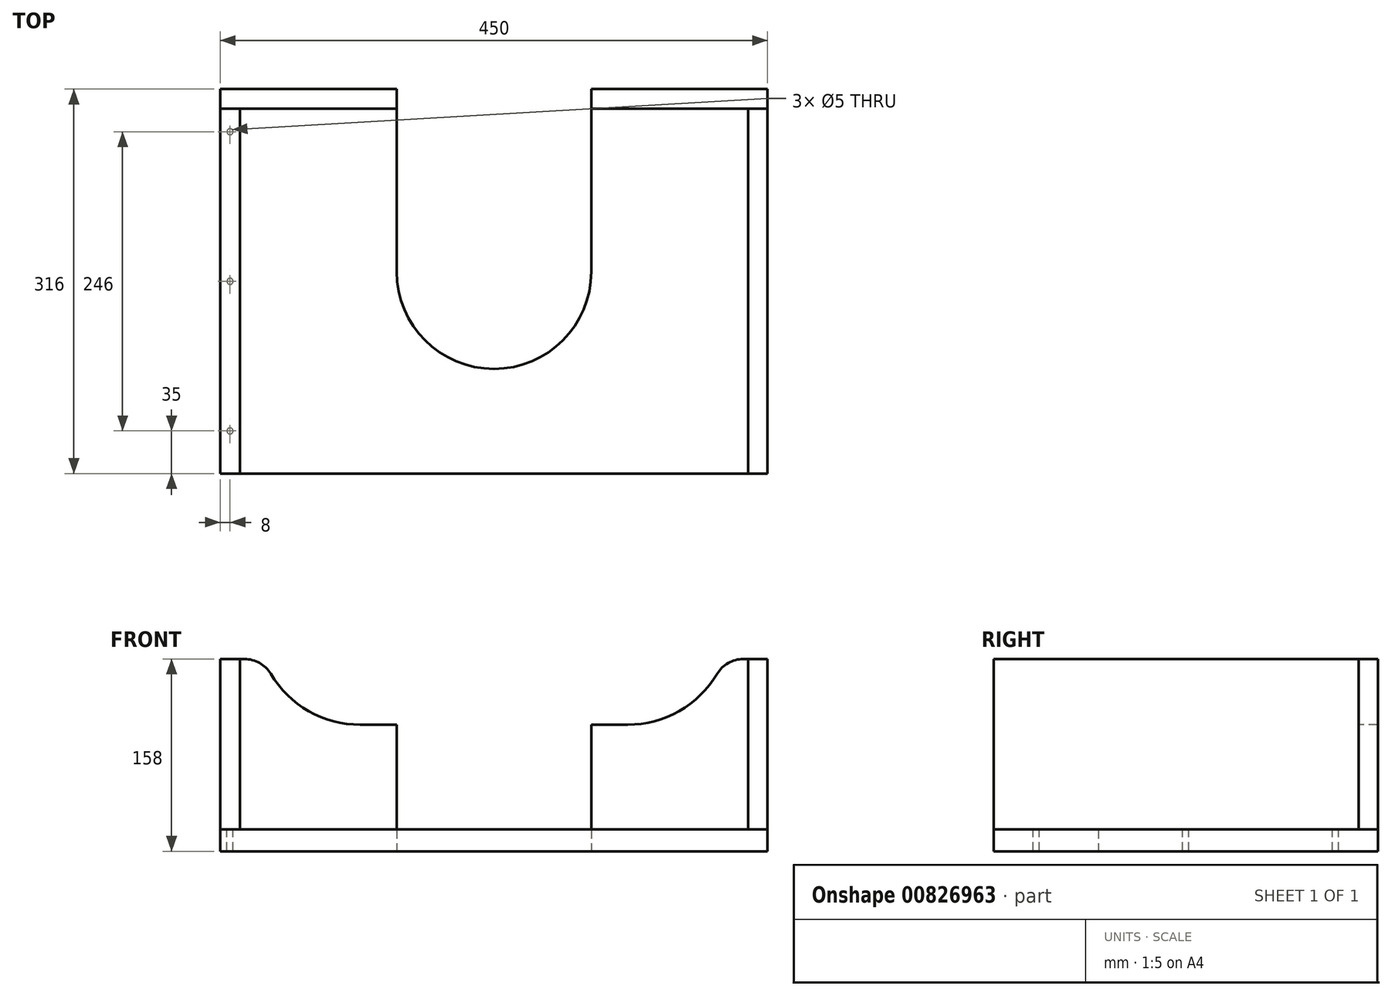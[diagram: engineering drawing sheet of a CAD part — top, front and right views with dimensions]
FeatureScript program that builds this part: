
annotation { "Feature Type Name" : "Feature", "Feature Type Description" : "" }
export const myFeature = defineFeature(function(context is Context, id is Id, definition is map)
    precondition{}
    {
        {
            var Q0;
            Q0=qCreatedBy(makeId("Front.planeOp"),FACE);
            var sketch = newSketch(context, id + "F0", { "sketchPlane" : qUnion([Q0])});
            skLineSegment(sketch, "E0.bottom", {"start": v(225, 70) * mm, "end": v(-225, 70) * mm});
            skLineSegment(sketch, "E0.top", {"start": v(225, -70) * mm, "end": v(-225, -70) * mm});
            skLineSegment(sketch, "E0.left", {"start": v(225, 70) * mm, "end": v(225, -70) * mm});
            skLineSegment(sketch, "E0.right", {"start": v(-225, 70) * mm, "end": v(-225, -70) * mm});
            skPoint(sketch, "E0.middle", {"position": v(0, 0) * mm});
            skSolve(sketch);
        }
        {
            var Q0;
            Q0=makeQuery(id+"F0.imprint","IMPRINT",FACE,{"disambiguationData":[TD([[makeQuery(id+"F0.imprint","IMPRINT",EDGE,{"derivedFrom":sQuery(id+"F0.wireOp",EDGE,"E0.bottom")}),1.0]])]});
            extrude(context, id + "F1", {"entities" : qUnion([Q0]), "depth" : 16 * mm, "offsetDistance" : 25 * mm});
        }
        {
            var Q0;
            Q0=makeQuery(id+"F1.opExtrude","CAP_FACE",FACE,{"disambiguationData":[OSD([sQuery(id+"F0.wireOp",EDGE,"E0.bottom"),sQuery(id+"F0.wireOp",EDGE,"E0.top"),sQuery(id+"F0.wireOp",EDGE,"E0.left"),sQuery(id+"F0.wireOp",EDGE,"E0.right")])],"isStart":false});
            var sketch = newSketch(context, id + "F2", { "sketchPlane" : qUnion([Q0])});
            skLineSegment(sketch, "E1", {"start": v(-225, 70) * mm, "end": v(-205, 70) * mm});
            skArc(sketch, "E2", {"start": v(-183.52, 57.79) * mm, "mid": v(-192.65, 66.73) * mm, "end": v(-205, 70) * mm});
            skArc(sketch, "E3", {"start": v(-183.52, 57.79) * mm, "mid": v(-152.28, 27.18) * mm, "end": v(-110, 16) * mm});
            skLineSegment(sketch, "E4", {"start": v(-110, 16) * mm, "end": v(0, 16) * mm});
            skLineSegment(sketch, "E5", {"start": v(0, 70) * mm, "end": v(0, -70) * mm, "construction": true});
            skLineSegment(sketch, "E6.MirrorCS", {"start": v(225, 70) * mm, "end": v(205, 70) * mm});
            skLineSegment(sketch, "E7.MirrorCS", {"start": v(110, 16) * mm, "end": v(0, 16) * mm});
            skArc(sketch, "E8.MirrorCS", {"start": v(183.52, 57.79) * mm, "mid": v(152.28, 27.18) * mm, "end": v(110, 16) * mm});
            skArc(sketch, "E9.MirrorCS", {"start": v(183.52, 57.79) * mm, "mid": v(192.65, 66.73) * mm, "end": v(205, 70) * mm});
            skSolve(sketch);
        }
        {
            var Q0;
            {var subQ0=sQuery(id+"F2.wireOp",EDGE,"E2");Q0=makeQuery(id+"F2.imprint","IMPRINT",FACE,{"disambiguationData":[TD([[makeQuery(id+"F2.imprint","IMPRINT",EDGE,{"derivedFrom":subQ0}),-1.0]])]});}
            extrude(context, id + "F3", {"entities" : qUnion([Q0]), "operationType" : NewBodyOperationType.REMOVE, "endBound" : BoundingType.THROUGH_ALL, "oppositeDirection" : true, "depth" : 25 * mm, "offsetDistance" : 25 * mm});
        }
        {
            var Q0;
            Q0=makeQuery(id+"F1.opExtrude","CAP_FACE",FACE,{"disambiguationData":[OSD([sQuery(id+"F0.wireOp",EDGE,"E0.bottom"),sQuery(id+"F0.wireOp",EDGE,"E0.top"),sQuery(id+"F0.wireOp",EDGE,"E0.left"),sQuery(id+"F0.wireOp",EDGE,"E0.right")])],"isStart":false});
            var sketch = newSketch(context, id + "F4", { "sketchPlane" : qUnion([Q0])});
            skLineSegment(sketch, "E10", {"start": v(-209, 70) * mm, "end": v(-209, -70) * mm});
            skSolve(sketch);
        }
        {
            var Q0;
            {var subQ0=sQuery(id+"F4.wireOp",EDGE,"E10");Q0=makeQuery(id+"F4.imprint","IMPRINT",FACE,{"disambiguationData":[TD([[makeQuery(id+"F4.imprint","IMPRINT",EDGE,{"derivedFrom":subQ0}),-1.0]])]});}
            extrude(context, id + "F5", {"entities" : qUnion([Q0]), "depth" : 300 * mm, "offsetDistance" : 25 * mm});
        }
        {
            var Q0;
            Q0=makeQuery(id+"F5.opExtrude","SWEPT_BODY",BODY,{"disambiguationData":[OSD([sQuery(id+"F0.wireOp",EDGE,"E0.bottom"),sQuery(id+"F0.wireOp",EDGE,"E0.top"),sQuery(id+"F0.wireOp",EDGE,"E0.right"),sQuery(id+"F4.wireOp",EDGE,"E10")])]});
            var Q1;
            Q1=qCreatedBy(makeId("Right.planeOp"),FACE);
            mirror(context, id + "F6", {"entities" : qUnion([Q0]), "mirrorPlane" : qUnion([Q1])});
        }
        {
            var Q0;
            Q0=makeQuery(id+"F1.opExtrude","SWEPT_FACE",FACE,{"disambiguationData":[OSD([sQuery(id+"F0.wireOp",EDGE,"E0.top")])]});
            var sketch = newSketch(context, id + "F7", { "sketchPlane" : qUnion([Q0])});
            skLineSegment(sketch, "E11.bottom", {"start": v(-225, 0) * mm, "end": v(225, 0) * mm});
            skLineSegment(sketch, "E11.top", {"start": v(-225, 316) * mm, "end": v(225, 316) * mm});
            skLineSegment(sketch, "E11.left", {"start": v(-225, 0) * mm, "end": v(-225, 316) * mm});
            skLineSegment(sketch, "E11.right", {"start": v(225, 0) * mm, "end": v(225, 316) * mm});
            skSolve(sketch);
        }
        {
            var Q0;
            Q0 = qSketchRegion(id + "F7", true);
            extrude(context, id + "F8", {"entities" : qUnion([Q0]), "depth" : 18 * mm, "offsetDistance" : 25 * mm});
        }
        {
            var Q0;
            Q0=makeQuery(id+"F8.opExtrude","CAP_FACE",FACE,{"disambiguationData":[OSD([sQuery(id+"F7.wireOp",EDGE,"E11.bottom"),sQuery(id+"F7.wireOp",EDGE,"E11.top"),sQuery(id+"F7.wireOp",EDGE,"E11.left"),sQuery(id+"F7.wireOp",EDGE,"E11.right")])],"isStart":true});
            var sketch = newSketch(context, id + "F9", { "sketchPlane" : qUnion([Q0])});
            skLineSegment(sketch, "E12", {"start": v(0, 0) * mm, "end": v(0, -316) * mm, "construction": true});
            skLineSegment(sketch, "E13", {"start": v(-80, 0) * mm, "end": v(-80, -150) * mm});
            skArc(sketch, "E14", {"start": v(-80, -150) * mm, "mid": v(0, -230) * mm, "end": v(80, -150) * mm});
            skLineSegment(sketch, "E15.MirrorCS", {"start": v(80, 0) * mm, "end": v(80, -150) * mm});
            skSolve(sketch);
        }
        {
            var Q0;
            Q0 = qSketchRegion(id + "F9", true);
            var Q1;
            {var subQ0=sQuery(id+"F9.wireOp",EDGE,"E13");Q1=makeQuery(id+"F9.imprint","IMPRINT",FACE,{"disambiguationData":[TD([[makeQuery(id+"F9.imprint","IMPRINT",EDGE,{"derivedFrom":subQ0}),1.0]])]});}
            extrude(context, id + "F10", {"entities" : qUnion([Q0, Q1]), "operationType" : NewBodyOperationType.REMOVE, "endBound" : BoundingType.SYMMETRIC, "depth" : 500 * mm, "offsetDistance" : 25 * mm});
        }
        {
            var Q0;
            Q0=makeQuery(id+"F8.opExtrude","CAP_FACE",FACE,{"disambiguationData":[OSD([sQuery(id+"F7.wireOp",EDGE,"E11.bottom"),sQuery(id+"F7.wireOp",EDGE,"E11.top"),sQuery(id+"F7.wireOp",EDGE,"E11.left"),sQuery(id+"F7.wireOp",EDGE,"E11.right")])],"isStart":true});
            var sketch = newSketch(context, id + "F11", { "sketchPlane" : qUnion([Q0])});
            skLineSegment(sketch, "E16", {"start": v(-217, 0) * mm, "end": v(-217, -316) * mm, "construction": true});
            skPoint(sketch, "E17", {"position": v(-217, -35) * mm});
            skPoint(sketch, "E18", {"position": v(-217, -158) * mm});
            skPoint(sketch, "E19", {"position": v(-217, -281) * mm});
            skSolve(sketch);
        }
        {
            var Q0;
            Q0=sQuery(id+"F11.wireOp",VERTEX,"E18");
            var Q1;
            Q1=sQuery(id+"F11.wireOp",VERTEX,"E19");
            var Q2;
            Q2=sQuery(id+"F11.wireOp",VERTEX,"E17");
            var Q3;
            Q3=makeQuery(id+"F8.opExtrude","SWEPT_BODY",BODY,{"disambiguationData":[OSD([sQuery(id+"F7.wireOp",EDGE,"E11.bottom"),sQuery(id+"F7.wireOp",EDGE,"E11.top"),sQuery(id+"F7.wireOp",EDGE,"E11.left"),sQuery(id+"F7.wireOp",EDGE,"E11.right")])]});
            hole(context, id + "F12", {"style" : HoleStyle.SIMPLE, "endStyle" : HoleEndStyle.THROUGH, "holeDiameter" : 5 * mm, "majorDiameter" : 5 * mm, "isTappedThrough" : true, "tappedDepth" : 12 * mm, "tapClearance" : 3, "locations" : qUnion([Q0, Q1, Q2]), "scope" : qUnion([Q3])});
        }
    });
